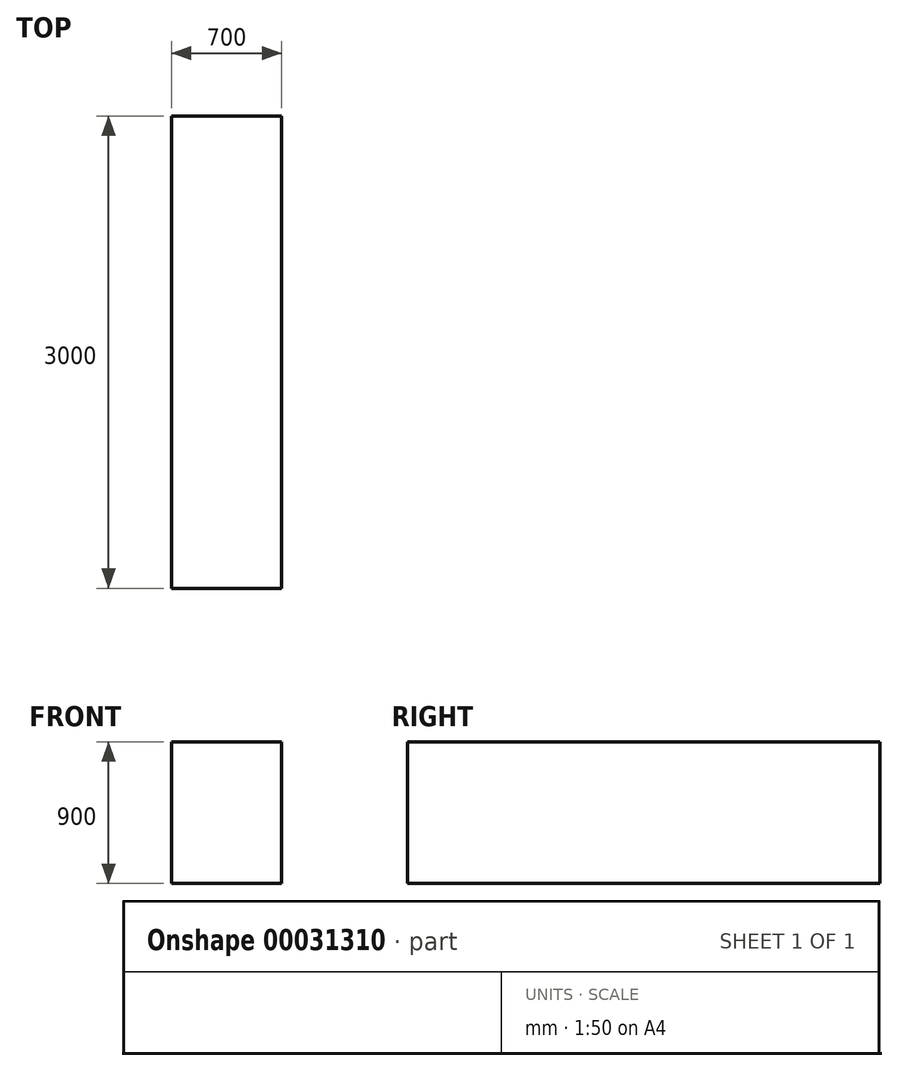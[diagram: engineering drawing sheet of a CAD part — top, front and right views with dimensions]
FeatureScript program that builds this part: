
annotation { "Feature Type Name" : "Feature", "Feature Type Description" : "" }
export const myFeature = defineFeature(function(context is Context, id is Id, definition is map)
    precondition{}
    {
        {
            var Q0;
            Q0=qCreatedBy(makeId("Front.planeOp"),FACE);
            var sketch = newSketch(context, id + "F0", { "sketchPlane" : qUnion([Q0])});
            skLineSegment(sketch, "E0.rect.bottom", {"start": v(350, 450) * mm, "end": v(-350, 450) * mm});
            skLineSegment(sketch, "E0.rect.top", {"start": v(350, -450) * mm, "end": v(-350, -450) * mm});
            skLineSegment(sketch, "E0.rect.left", {"start": v(350, 450) * mm, "end": v(350, -450) * mm});
            skLineSegment(sketch, "E0.rect.right", {"start": v(-350, 450) * mm, "end": v(-350, -450) * mm});
            skPoint(sketch, "E0.rect.middle", {"position": v(0, 0) * mm});
            skSolve(sketch);
        }
        {
            var Q0;
            Q0=makeQuery(id+"F0.imprint","IMPRINT",FACE,{"disambiguationData":[TD([[makeQuery(id+"F0.imprint","IMPRINT",EDGE,{"derivedFrom":sQuery(id+"F0.wireOp",EDGE,"E0.rect.bottom")}),1.0]])]});
            extrude(context, id + "F1", {"entities" : qUnion([Q0]), "endBound" : BoundingType.SYMMETRIC, "depth" : 3000 * mm});
        }
    });
